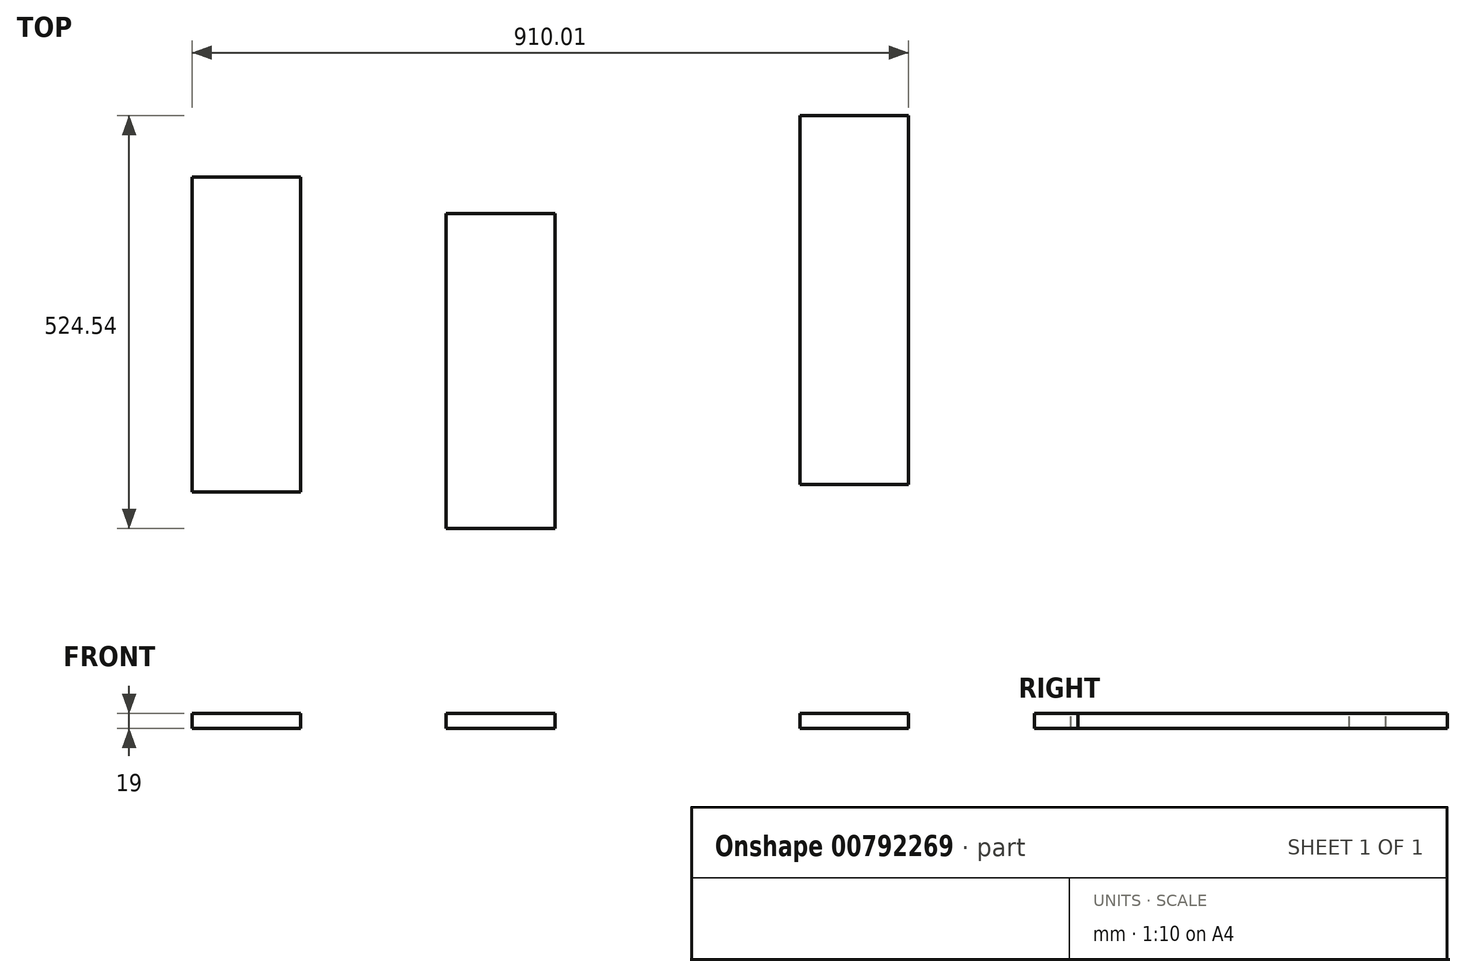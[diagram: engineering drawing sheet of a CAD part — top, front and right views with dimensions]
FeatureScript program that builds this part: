
annotation { "Feature Type Name" : "Feature", "Feature Type Description" : "" }
export const myFeature = defineFeature(function(context is Context, id is Id, definition is map)
    precondition{}
    {
        {
            var Q0;
            Q0=qCreatedBy(makeId("Top.planeOp"),FACE);
            var sketch = newSketch(context, id + "F0", { "sketchPlane" : qUnion([Q0])});
            skLineSegment(sketch, "E0.bottom", {"start": v(-460.76, -262) * mm, "end": v(-322.76, -262) * mm});
            skLineSegment(sketch, "E0.top", {"start": v(-460.76, 138) * mm, "end": v(-322.76, 138) * mm});
            skLineSegment(sketch, "E0.left", {"start": v(-460.76, -262) * mm, "end": v(-460.76, 138) * mm});
            skLineSegment(sketch, "E0.right", {"start": v(-322.76, -262) * mm, "end": v(-322.76, 138) * mm});
            skLineSegment(sketch, "E1.bottom", {"start": v(0, -308.35) * mm, "end": v(-138, -308.35) * mm});
            skLineSegment(sketch, "E1.top", {"start": v(0, 91.65) * mm, "end": v(-138, 91.65) * mm});
            skLineSegment(sketch, "E1.left", {"start": v(0, -308.35) * mm, "end": v(0, 91.65) * mm});
            skLineSegment(sketch, "E1.right", {"start": v(-138, -308.35) * mm, "end": v(-138, 91.65) * mm});
            skLineSegment(sketch, "E2.bottom", {"start": v(449.25, -252.78) * mm, "end": v(311.25, -252.78) * mm});
            skLineSegment(sketch, "E2.top", {"start": v(449.25, 216.19) * mm, "end": v(311.25, 216.19) * mm});
            skLineSegment(sketch, "E2.left", {"start": v(449.25, -252.78) * mm, "end": v(449.25, 216.19) * mm});
            skLineSegment(sketch, "E2.right", {"start": v(311.25, -252.78) * mm, "end": v(311.25, 216.19) * mm});
            skSolve(sketch);
        }
        {
            var Q0;
            Q0=sQuery(id+"F0.wireOp",EDGE,"E2.right");
            var Q1;
            Q1=sQuery(id+"F0.wireOp",EDGE,"E2.left");
            var Q2;
            Q2=sQuery(id+"F0.wireOp",EDGE,"E2.top");
            var Q3;
            Q3=sQuery(id+"F0.wireOp",EDGE,"E2.bottom");
            var Q4;
            Q4=sQuery(id+"F0.wireOp",EDGE,"E1.right");
            var Q5;
            Q5=sQuery(id+"F0.wireOp",EDGE,"E1.left");
            var Q6;
            Q6=sQuery(id+"F0.wireOp",EDGE,"E1.top");
            var Q7;
            Q7=sQuery(id+"F0.wireOp",EDGE,"E1.bottom");
            var Q8;
            Q8=sQuery(id+"F0.wireOp",EDGE,"E0.right");
            var Q9;
            Q9=sQuery(id+"F0.wireOp",EDGE,"E0.left");
            var Q10;
            Q10=sQuery(id+"F0.wireOp",EDGE,"E0.top");
            var Q11;
            Q11=sQuery(id+"F0.wireOp",EDGE,"E0.bottom");
            extrude(context, id + "F1", {"bodyType" : ToolBodyType.SURFACE, "surfaceEntities" : qUnion([Q0, Q1, Q2, Q3, Q4, Q5, Q6, Q7, Q8, Q9, Q10, Q11]), "depth" : 19 * mm, "offsetDistance" : 25 * mm});
        }
    });
